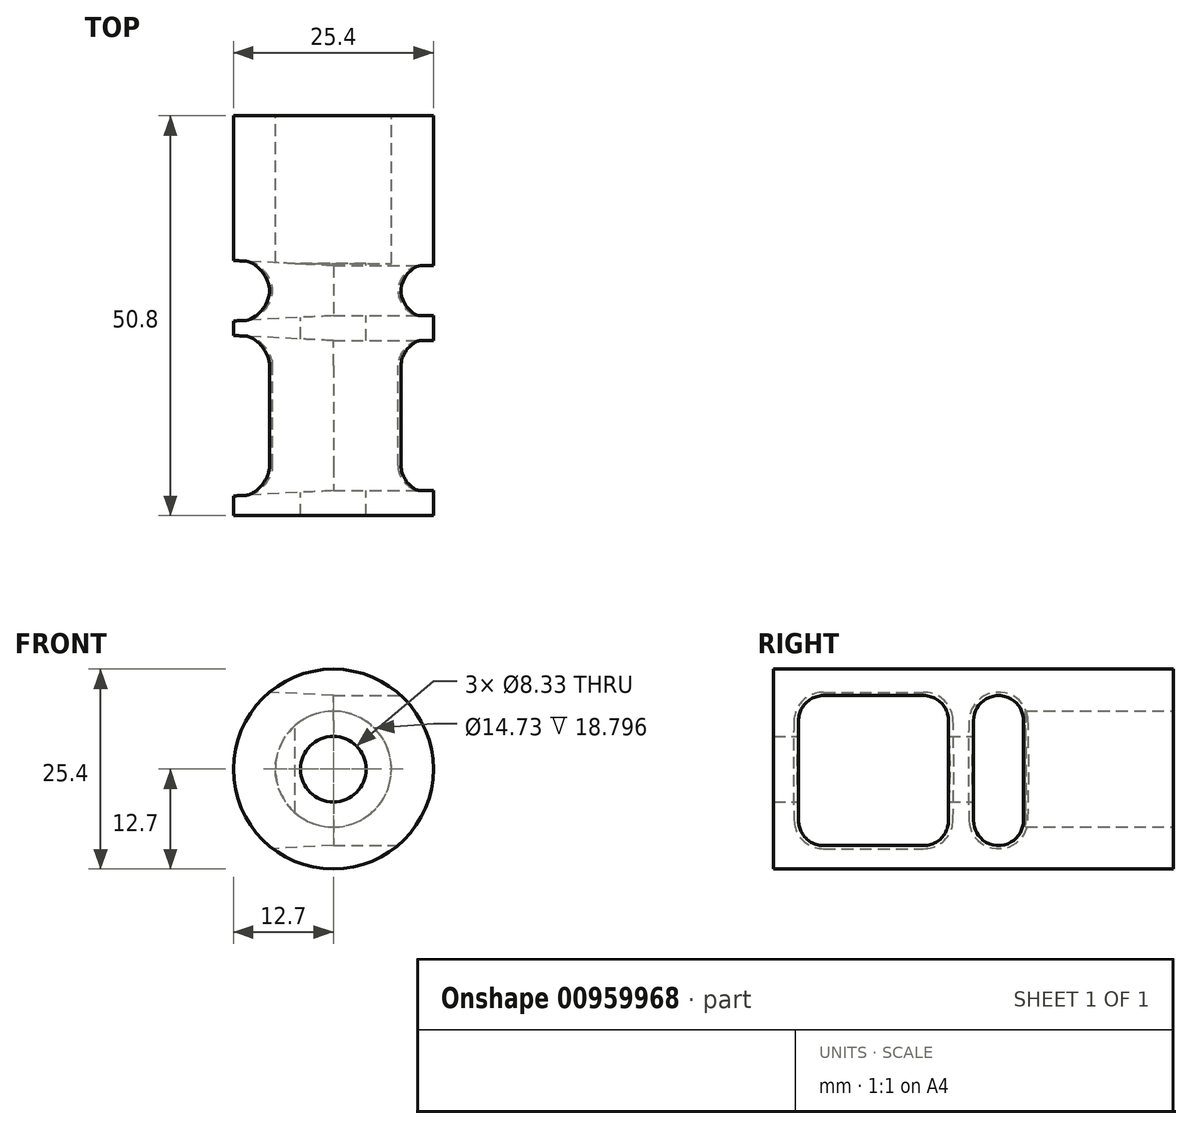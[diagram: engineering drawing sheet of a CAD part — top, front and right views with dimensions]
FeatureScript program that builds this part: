
annotation { "Feature Type Name" : "Feature", "Feature Type Description" : "" }
export const myFeature = defineFeature(function(context is Context, id is Id, definition is map)
    precondition{}
    {
        {
            var Q0;
            Q0=qCreatedBy(makeId("Front.planeOp"),FACE);
            var sketch = newSketch(context, id + "F0", { "sketchPlane" : qUnion([Q0])});
            skCircle(sketch, "E0", {"center": v(0, 0) * mm, "radius": 12.7 * mm});
            skSolve(sketch);
        }
        {
            var Q0;
            Q0=makeQuery(id+"F0.imprint","IMPRINT",FACE,{"disambiguationData":[TD([[makeQuery(id+"F0.imprint","IMPRINT",EDGE,{"derivedFrom":sQuery(id+"F0.wireOp",EDGE,"E0")}),1.0]])]});
            var sketch = newSketch(context, id + "F1", { "sketchPlane" : qUnion([Q0])});
            skCircle(sketch, "E1", {"center": v(0, 0) * mm, "radius": 7.37 * mm});
            skCircle(sketch, "E2", {"center": v(0, 0) * mm, "radius": 4.17 * mm});
            skSolve(sketch);
        }
        {
            var Q0;
            Q0=makeQuery(id+"F1.imprint","IMPRINT",FACE,{"disambiguationData":[TD([[makeQuery(id+"F1.imprint","IMPRINT",EDGE,{"derivedFrom":sQuery(id+"F1.wireOp",EDGE,"E1")}),-1.0]])]});
            var Q1;
            Q1=makeQuery(id+"F0.imprint","IMPRINT",FACE,{"disambiguationData":[TD([[makeQuery(id+"F0.imprint","IMPRINT",EDGE,{"derivedFrom":sQuery(id+"F0.wireOp",EDGE,"E0")}),1.0]])]});
            extrude(context, id + "F2", {"entities" : qUnion([Q0, Q1]), "depth" : 50.8 * mm, "offsetDistance" : 25.4 * mm});
        }
        {
            var Q0;
            Q0=makeQuery(id+"F1.imprint","IMPRINT",FACE,{"disambiguationData":[TD([[makeQuery(id+"F1.imprint","IMPRINT",EDGE,{"derivedFrom":sQuery(id+"F1.wireOp",EDGE,"E2")}),1.0]])]});
            extrude(context, id + "F3", {"entities" : qUnion([Q0]), "operationType" : NewBodyOperationType.REMOVE, "endBound" : BoundingType.THROUGH_ALL, "depth" : 25.4 * mm, "offsetDistance" : 25.4 * mm});
        }
        {
            var Q0;
            Q0=makeQuery(id+"F1.imprint","IMPRINT",FACE,{"disambiguationData":[TD([[makeQuery(id+"F1.imprint","IMPRINT",EDGE,{"derivedFrom":sQuery(id+"F1.wireOp",EDGE,"E1")}),1.0]])]});
            extrude(context, id + "F4", {"entities" : qUnion([Q0]), "operationType" : NewBodyOperationType.REMOVE, "depth" : 18.8 * mm, "offsetDistance" : 25.4 * mm});
        }
        {
            var Q0;
            Q0=qCreatedBy(makeId("Right.planeOp"),FACE);
            var sketch = newSketch(context, id + "F5", { "sketchPlane" : qUnion([Q0])});
            skLineSegment(sketch, "E3", {"start": v(-47.63, 6.17) * mm, "end": v(-47.63, -6.53) * mm});
            skArc(sketch, "E4", {"start": v(-47.62, 6.17) * mm, "mid": v(-46.7, 8.42) * mm, "end": v(-44.45, 9.35) * mm});
            skLineSegment(sketch, "E5", {"start": v(-44.45, 9.35) * mm, "end": v(-31.75, 9.35) * mm});
            skArc(sketch, "E6", {"start": v(-31.75, 9.35) * mm, "mid": v(-29.5, 8.42) * mm, "end": v(-28.58, 6.17) * mm});
            skArc(sketch, "E7", {"start": v(-47.63, -6.53) * mm, "mid": v(-46.7, -8.77) * mm, "end": v(-44.45, -9.7) * mm});
            skLineSegment(sketch, "E8", {"start": v(-44.45, -9.7) * mm, "end": v(-31.75, -9.7) * mm});
            skLineSegment(sketch, "E9", {"start": v(-28.58, 6.17) * mm, "end": v(-28.58, -6.53) * mm});
            skArc(sketch, "E10", {"start": v(-31.75, -9.7) * mm, "mid": v(-29.5, -8.77) * mm, "end": v(-28.58, -6.53) * mm});
            skLineSegment(sketch, "E11", {"start": v(-25.4, 6.17) * mm, "end": v(-25.4, -6.53) * mm});
            skLineSegment(sketch, "E12", {"start": v(-19.05, 6.17) * mm, "end": v(-19.05, -6.53) * mm});
            skArc(sketch, "E13", {"start": v(-25.4, 6.17) * mm, "mid": v(-24.47, 8.42) * mm, "end": v(-22.23, 9.35) * mm});
            skArc(sketch, "E14", {"start": v(-19.05, 6.17) * mm, "mid": v(-19.98, 8.42) * mm, "end": v(-22.23, 9.35) * mm});
            skArc(sketch, "E15", {"start": v(-25.4, -6.53) * mm, "mid": v(-24.47, -8.77) * mm, "end": v(-22.23, -9.7) * mm});
            skArc(sketch, "E16", {"start": v(-19.05, -6.53) * mm, "mid": v(-19.98, -8.77) * mm, "end": v(-22.23, -9.7) * mm});
            skSolve(sketch);
        }
        {
            var Q0;
            Q0=makeQuery(id+"F2.opExtrude","SWEPT_BODY",BODY,{"disambiguationData":[OSD([sQuery(id+"F0.wireOp",EDGE,"E0"),sQuery(id+"F1.wireOp",EDGE,"E1")])]});
            deleteBodies(context, id + "F6", {"entities" : qUnion([Q0])});
        }
        {
            var Q0;
            Q0 = qSketchRegion(id + "F5", true);
            extrude(context, id + "F7", {"entities" : qUnion([Q0]), "operationType" : NewBodyOperationType.REMOVE, "endBound" : BoundingType.THROUGH_ALL, "oppositeDirection" : true, "depth" : 25.4 * mm, "offsetDistance" : 25.4 * mm, "hasDraft" : true, "draftAngle" : 3 * degree, "hasSecondDirection" : true, "secondDirectionOppositeDirection" : false, "secondDirectionDepth" : 25.4 * mm});
        }
    });
